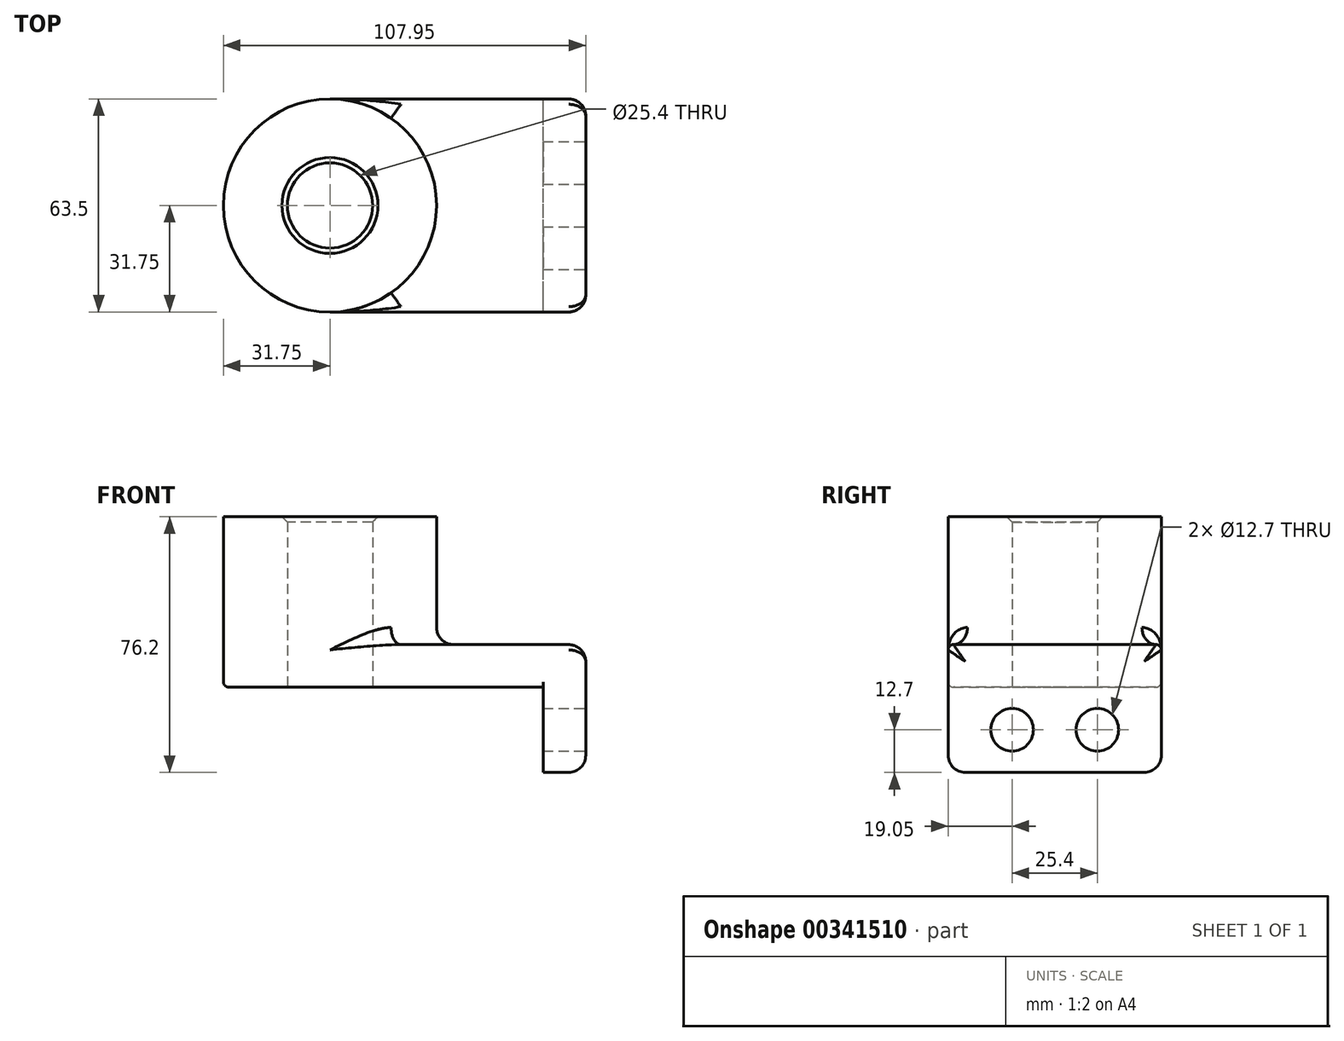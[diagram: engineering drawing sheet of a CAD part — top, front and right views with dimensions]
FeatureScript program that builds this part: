
annotation { "Feature Type Name" : "Feature", "Feature Type Description" : "" }
export const myFeature = defineFeature(function(context is Context, id is Id, definition is map)
    precondition{}
    {
        {
            var Q0;
            Q0=qCreatedBy(makeId("Top.planeOp"),FACE);
            var sketch = newSketch(context, id + "F0", { "sketchPlane" : qUnion([Q0])});
            skLineSegment(sketch, "E0.bottom", {"start": v(-38.1, -31.75) * mm, "end": v(38.1, -31.75) * mm});
            skLineSegment(sketch, "E0.top", {"start": v(-38.1, 31.75) * mm, "end": v(38.1, 31.75) * mm});
            skLineSegment(sketch, "E0.left", {"start": v(-38.1, -31.75) * mm, "end": v(-38.1, 31.75) * mm});
            skLineSegment(sketch, "E0.right", {"start": v(38.1, -31.75) * mm, "end": v(38.1, 31.75) * mm});
            skPoint(sketch, "E0.middle", {"position": v(0, 0) * mm});
            skCircle(sketch, "E1", {"center": v(-38.1, 0) * mm, "radius": 31.75 * mm});
            skCircle(sketch, "E2", {"center": v(-38.1, 0) * mm, "radius": 12.7 * mm});
            skSolve(sketch);
        }
        {
            var Q0;
            Q0 = qSketchRegion(id + "F0", true);
            extrude(context, id + "F1", {"entities" : qUnion([Q0]), "depth" : 12.7 * mm});
        }
        {
            var Q0;
            {var subQ1=sQuery(id+"F0.wireOp",EDGE,"E0.left");var subQ3=sQuery(id+"F0.wireOp",EDGE,"E2");var subQ4=makeQuery(id+"F0.imprint","INTERSECT",VERTEX,{"disambiguationData":[OD(0.0)],"derivedFrom":[subQ1,subQ3]});Q0=makeQuery(id+"F0.imprint","IMPRINT",FACE,{"disambiguationData":[TD([[makeQuery(id+"F0.imprint","IMPRINT",EDGE,{"disambiguationData":[TD([[subQ4,1.0]])],"derivedFrom":subQ3}),-1.0]])]});}
            var Q1;
            {var subQ1=sQuery(id+"F0.wireOp",EDGE,"E0.left");var subQ3=sQuery(id+"F0.wireOp",EDGE,"E2");var subQ4=makeQuery(id+"F0.imprint","INTERSECT",VERTEX,{"disambiguationData":[OD(0.0)],"derivedFrom":[subQ1,subQ3]});Q1=makeQuery(id+"F0.imprint","IMPRINT",FACE,{"disambiguationData":[TD([[makeQuery(id+"F0.imprint","IMPRINT",EDGE,{"disambiguationData":[TD([[subQ4,-1.0]])],"derivedFrom":subQ3}),-1.0]])]});}
            extrude(context, id + "F2", {"entities" : qUnion([Q0, Q1]), "operationType" : NewBodyOperationType.ADD, "depth" : 50.8 * mm});
        }
        {
            var Q0;
            Q0=makeQuery(id+"F1.opExtrude","SWEPT_FACE",FACE,{"disambiguationData":[OSD([sQuery(id+"F0.wireOp",EDGE,"E0.right")])]});
            var sketch = newSketch(context, id + "F3", { "sketchPlane" : qUnion([Q0])});
            skLineSegment(sketch, "E3.bottom", {"start": v(-31.75, 12.7) * mm, "end": v(31.75, 12.7) * mm});
            skLineSegment(sketch, "E3.top", {"start": v(-31.75, -25.4) * mm, "end": v(31.75, -25.4) * mm});
            skLineSegment(sketch, "E3.left", {"start": v(-31.75, 12.7) * mm, "end": v(-31.75, -25.4) * mm});
            skLineSegment(sketch, "E3.right", {"start": v(31.75, 12.7) * mm, "end": v(31.75, -25.4) * mm});
            skCircle(sketch, "E4", {"center": v(-12.7, -12.7) * mm, "radius": 6.35 * mm});
            skLineSegment(sketch, "E5", {"start": v(0, -1.84) * mm, "end": v(0, -25.4) * mm});
            skCircle(sketch, "E6.MirrorC", {"center": v(12.7, -12.7) * mm, "radius": 6.35 * mm});
            skSolve(sketch);
        }
        {
            var Q0;
            Q0 = qSketchRegion(id + "F3", true);
            extrude(context, id + "F4", {"entities" : qUnion([Q0]), "operationType" : NewBodyOperationType.ADD, "oppositeDirection" : true, "depth" : 12.7 * mm});
        }
        {
            var Q0;
            Q0=makeQuery(id+"F1.opExtrude","CAP_EDGE",EDGE,{"disambiguationData":[OSD([sQuery(id+"F0.wireOp",EDGE,"E0.bottom")])],"isStart":false});
            var Q1;
            Q1=makeQuery(id+"F1.opExtrude","CAP_EDGE",EDGE,{"disambiguationData":[OSD([sQuery(id+"F0.wireOp",EDGE,"E0.bottom")])],"isStart":true});
            var Q2;
            Q2=makeQuery(id+"F1.opExtrude","CAP_EDGE",EDGE,{"disambiguationData":[OSD([sQuery(id+"F0.wireOp",EDGE,"E0.top")])],"isStart":false});
            var Q3;
            Q3=makeQuery(id+"F1.opExtrude","CAP_EDGE",EDGE,{"disambiguationData":[OSD([sQuery(id+"F0.wireOp",EDGE,"E0.top")])],"isStart":true});
            fillet(context, id + "F5", {"entities" : qUnion([Q0, Q1, Q2, Q3]), "radius" : 1.59 * mm, "tangentPropagation" : true, "allowEdgeOverflow" : false});
        }
        {
            var Q0;
            Q0=makeQuery(id+"F4.opExtrude","SWEPT_EDGE",EDGE,{"disambiguationData":[OSD([sQuery(id+"F3.wireOp",EDGE,"E3.top"),sQuery(id+"F3.wireOp",EDGE,"E3.left")])]});
            var Q1;
            Q1=makeQuery(id+"F4.opExtrude","CAP_EDGE",EDGE,{"disambiguationData":[OSD([sQuery(id+"F3.wireOp",EDGE,"E3.top")])],"isStart":true});
            var Q2;
            Q2=makeQuery(id+"F4.opExtrude","SWEPT_EDGE",EDGE,{"disambiguationData":[OSD([sQuery(id+"F3.wireOp",EDGE,"E3.top"),sQuery(id+"F3.wireOp",EDGE,"E3.right")])]});
            var Q3;
            Q3=makeQuery(id+"F1.opExtrude","CAP_EDGE",EDGE,{"disambiguationData":[OSD([sQuery(id+"F0.wireOp",EDGE,"E0.right")])],"isStart":false});
            var Q4;
            {var subQ0=sQuery(id+"F0.wireOp",EDGE,"E1");Q4=makeQuery(id+"F2.boolean.opBoolean","INTERSECT",EDGE,{"derivedFrom":[makeQuery(id+"F1.opExtrude","CAP_FACE",FACE,{"disambiguationData":[OSD([sQuery(id+"F0.wireOp",EDGE,"E0.bottom"),sQuery(id+"F0.wireOp",EDGE,"E0.top"),sQuery(id+"F0.wireOp",EDGE,"E0.right"),subQ0,sQuery(id+"F0.wireOp",EDGE,"E2")])],"isStart":false}),makeQuery(id+"F2.opExtrude","SWEPT_FACE",FACE,{"disambiguationData":[OSD([subQ0])]})]});}
            fillet(context, id + "F6", {"entities" : qUnion([Q0, Q1, Q2, Q3, Q4]), "radius" : 5.08 * mm, "tangentPropagation" : true, "allowEdgeOverflow" : false});
        }
        {
            var Q0;
            Q0=makeQuery(id+"F2.opExtrude","CAP_EDGE",EDGE,{"disambiguationData":[OSD([sQuery(id+"F0.wireOp",EDGE,"E2")])],"isStart":false});
            chamfer(context, id + "F7", {"entities" : qUnion([Q0]), "width" : 1.59 * mm, "tangentPropagation" : true});
        }
    });
